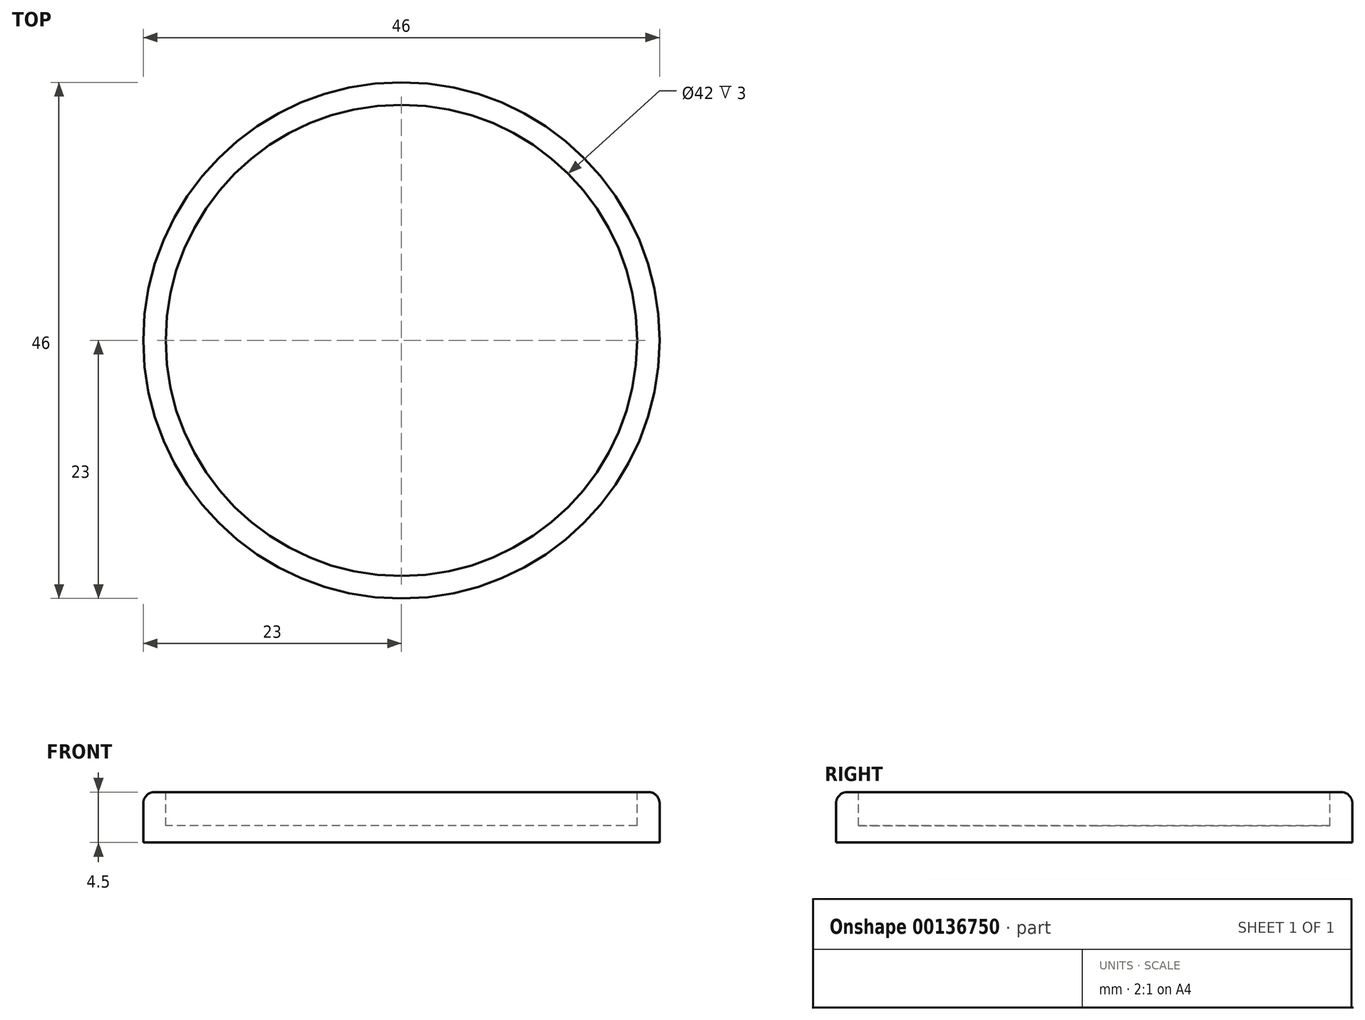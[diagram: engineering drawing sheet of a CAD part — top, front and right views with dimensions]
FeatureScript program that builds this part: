
annotation { "Feature Type Name" : "Feature", "Feature Type Description" : "" }
export const myFeature = defineFeature(function(context is Context, id is Id, definition is map)
    precondition{}
    {
        {
            var Q0;
            Q0=qCreatedBy(makeId("Top.planeOp"),FACE);
            var sketch = newSketch(context, id + "F0", { "sketchPlane" : qUnion([Q0])});
            skCircle(sketch, "E0", {"center": v(0, 0) * mm, "radius": 21 * mm});
            skCircle(sketch, "E1", {"center": v(0, 0) * mm, "radius": 23 * mm});
            skSolve(sketch);
        }
        {
            var Q0;
            Q0=makeQuery(id+"F0.imprint","IMPRINT",FACE,{"disambiguationData":[TD([[makeQuery(id+"F0.imprint","IMPRINT",EDGE,{"derivedFrom":sQuery(id+"F0.wireOp",EDGE,"E0")}),-1.0]])]});
            var Q1;
            Q1=makeQuery(id+"F0.imprint","IMPRINT",FACE,{"disambiguationData":[TD([[makeQuery(id+"F0.imprint","IMPRINT",EDGE,{"derivedFrom":sQuery(id+"F0.wireOp",EDGE,"E0")}),1.0]])]});
            extrude(context, id + "F1", {"entities" : qUnion([Q0, Q1]), "oppositeDirection" : true, "depth" : 4.5 * mm, "offsetDistance" : 25 * mm});
        }
        {
            var Q0;
            Q0=makeQuery(id+"F0.imprint","IMPRINT",FACE,{"disambiguationData":[TD([[makeQuery(id+"F0.imprint","IMPRINT",EDGE,{"derivedFrom":sQuery(id+"F0.wireOp",EDGE,"E0")}),1.0]])]});
            extrude(context, id + "F2", {"entities" : qUnion([Q0]), "operationType" : NewBodyOperationType.REMOVE, "oppositeDirection" : true, "depth" : 3 * mm, "offsetDistance" : 25 * mm});
        }
        {
            var Q0;
            Q0=makeQuery(id+"F2.boolean.opBoolean","COPY",EDGE,{"derivedFrom":makeQuery(id+"F2.opExtrude","CAP_EDGE",EDGE,{"disambiguationData":[OSD([sQuery(id+"F0.wireOp",EDGE,"E0")])],"isStart":true})});
            var Q1;
            Q1=makeQuery(id+"F1.opExtrude","CAP_EDGE",EDGE,{"disambiguationData":[OSD([sQuery(id+"F0.wireOp",EDGE,"E1")])],"isStart":true});
            fillet(context, id + "F3", {"entities" : qUnion([Q0, Q1]), "tangentPropagation" : true, "radius" : 1 * mm, "defaultsChanged" : true, "vertexSettings" : [], "allowEdgeOverflow" : false});
        }
    });
